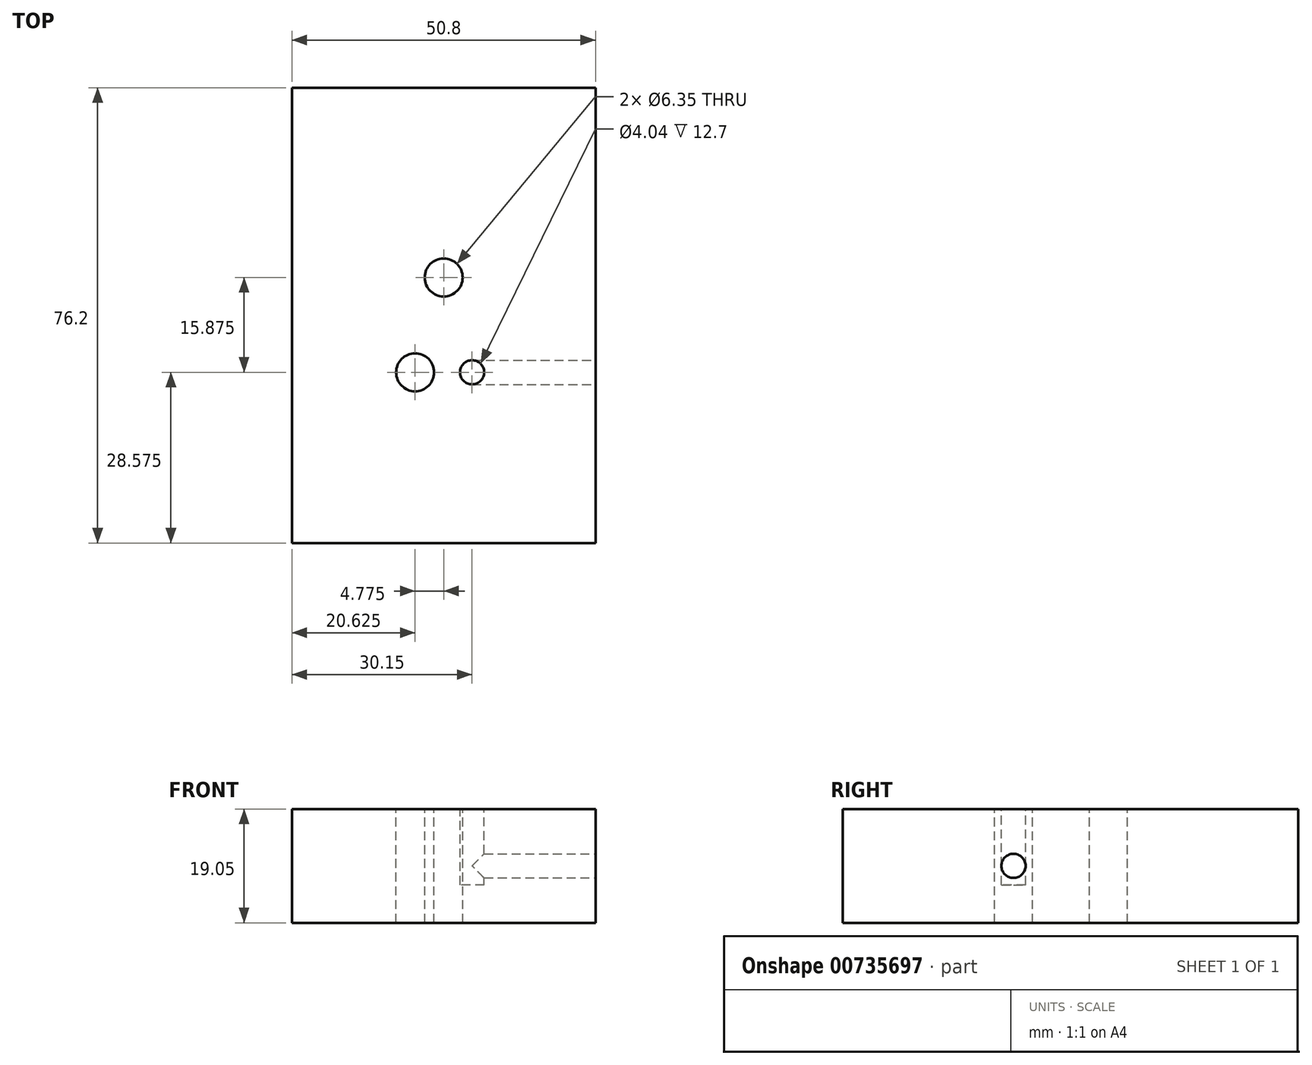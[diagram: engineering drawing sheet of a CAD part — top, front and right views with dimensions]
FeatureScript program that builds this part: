
annotation { "Feature Type Name" : "Feature", "Feature Type Description" : "" }
export const myFeature = defineFeature(function(context is Context, id is Id, definition is map)
    precondition{}
    {
        {
            var Q0;
            Q0=qCreatedBy(makeId("Top.planeOp"),FACE);
            var sketch = newSketch(context, id + "F0", { "sketchPlane" : qUnion([Q0])});
            skLineSegment(sketch, "E0.bottom", {"start": v(0, 0) * mm, "end": v(50.8, 0) * mm});
            skLineSegment(sketch, "E0.top", {"start": v(0, 76.2) * mm, "end": v(50.8, 76.2) * mm});
            skLineSegment(sketch, "E0.left", {"start": v(0, 0) * mm, "end": v(0, 76.2) * mm});
            skLineSegment(sketch, "E0.right", {"start": v(50.8, 0) * mm, "end": v(50.8, 76.2) * mm});
            skSolve(sketch);
        }
        {
            var Q0;
            Q0 = qSketchRegion(id + "F0", true);
            extrude(context, id + "F1", {"entities" : qUnion([Q0]), "depth" : 19.05 * mm, "offsetDistance" : 25.4 * mm});
        }
        {
            var Q0;
            Q0=makeQuery(id+"F1.opExtrude","CAP_FACE",FACE,{"disambiguationData":[OSD([sQuery(id+"F0.wireOp",EDGE,"E0.bottom"),sQuery(id+"F0.wireOp",EDGE,"E0.top"),sQuery(id+"F0.wireOp",EDGE,"E0.left"),sQuery(id+"F0.wireOp",EDGE,"E0.right")])],"isStart":false});
            var sketch = newSketch(context, id + "F2", { "sketchPlane" : qUnion([Q0])});
            skPoint(sketch, "E1", {"position": v(25.4, 0) * mm});
            skPoint(sketch, "E2", {"position": v(25.4, 44.45) * mm});
            skCircle(sketch, "E3", {"center": v(25.4, 44.45) * mm, "radius": 3.18 * mm});
            skPoint(sketch, "E4", {"position": v(20.62, 0) * mm});
            skPoint(sketch, "E5", {"position": v(37.9, 0) * mm});
            skPoint(sketch, "E6", {"position": v(50.8, 0) * mm});
            skPoint(sketch, "E7", {"position": v(20.62, 28.58) * mm});
            skCircle(sketch, "E8", {"center": v(20.62, 28.58) * mm, "radius": 3.18 * mm});
            skCircle(sketch, "E9", {"center": v(30.15, 28.58) * mm, "radius": 2.02 * mm});
            skSolve(sketch);
        }
        {
            var Q0;
            Q0=makeQuery(id+"F2.imprint","IMPRINT",FACE,{"disambiguationData":[TD([[makeQuery(id+"F2.imprint","IMPRINT",EDGE,{"derivedFrom":sQuery(id+"F2.wireOp",EDGE,"E3")}),1.0]])]});
            var Q1;
            Q1=makeQuery(id+"F2.imprint","IMPRINT",FACE,{"disambiguationData":[TD([[makeQuery(id+"F2.imprint","IMPRINT",EDGE,{"derivedFrom":sQuery(id+"F2.wireOp",EDGE,"E8")}),1.0]])]});
            var Q2;
            Q2=sQuery(id+"F2.wireOp",EDGE,"E3");
            extrude(context, id + "F3", {"entities" : qUnion([Q0, Q1]), "operationType" : NewBodyOperationType.REMOVE, "surfaceEntities" : qUnion([Q2]), "oppositeDirection" : true, "depth" : 19.05 * mm, "offsetDistance" : 25.4 * mm});
        }
        {
            var Q0;
            Q0 = qSketchRegion(id + "F2", true);
            extrude(context, id + "F4", {"entities" : qUnion([Q0]), "operationType" : NewBodyOperationType.REMOVE, "oppositeDirection" : true, "depth" : 12.7 * mm, "offsetDistance" : 25.4 * mm});
        }
        {
            var Q0;
            Q0=makeQuery(id+"F1.opExtrude","SWEPT_FACE",FACE,{"disambiguationData":[OSD([sQuery(id+"F0.wireOp",EDGE,"E0.right")])]});
            var sketch = newSketch(context, id + "F5", { "sketchPlane" : qUnion([Q0])});
            skPoint(sketch, "E10", {"position": v(0, 9.53) * mm});
            skPoint(sketch, "E11", {"position": v(28.57, 9.53) * mm});
            skCircle(sketch, "E12", {"center": v(28.57, 9.53) * mm, "radius": 2.02 * mm});
            skSolve(sketch);
        }
        {
            var Q0;
            Q0 = qSketchRegion(id + "F5", true);
            extrude(context, id + "F6", {"entities" : qUnion([Q0]), "operationType" : NewBodyOperationType.REMOVE, "oppositeDirection" : true, "depth" : 20.65 * mm, "offsetDistance" : 25.4 * mm});
        }
    });
